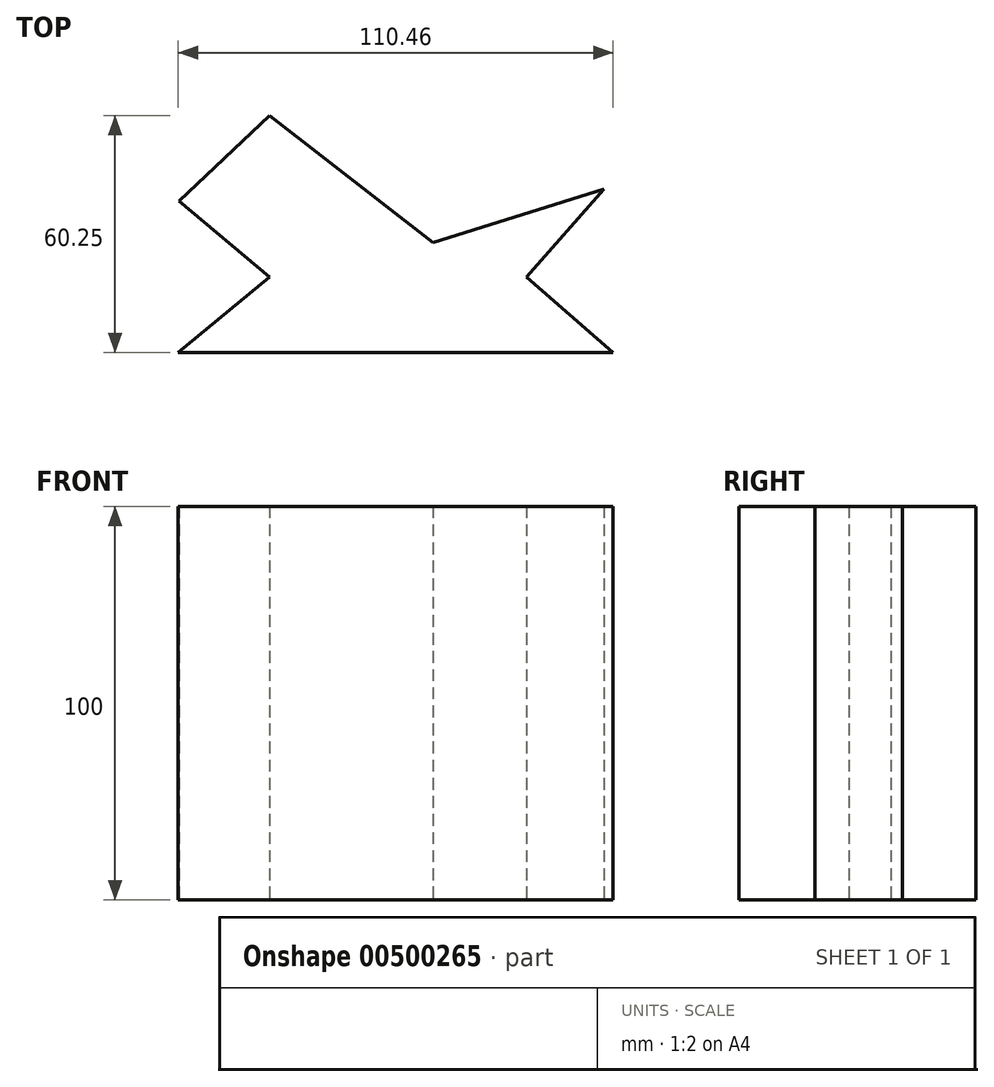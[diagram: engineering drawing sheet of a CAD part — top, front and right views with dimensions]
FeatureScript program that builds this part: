
annotation { "Feature Type Name" : "Feature", "Feature Type Description" : "" }
export const myFeature = defineFeature(function(context is Context, id is Id, definition is map)
    precondition{}
    {
        {
            var Q0;
            Q0=qCreatedBy(makeId("Top.planeOp"),FACE);
            var sketch = newSketch(context, id + "F0", { "sketchPlane" : qUnion([Q0])});
            skLineSegment(sketch, "E0", {"start": v(-41.49, 0) * mm, "end": v(-64.74, -19.3) * mm});
            skLineSegment(sketch, "E1", {"start": v(-41.49, 0) * mm, "end": v(-64.48, 19.3) * mm});
            skLineSegment(sketch, "E2", {"start": v(-64.74, -19.3) * mm, "end": v(45.72, -19.3) * mm});
            skLineSegment(sketch, "E3", {"start": v(45.72, -19.3) * mm, "end": v(23.78, 0) * mm});
            skLineSegment(sketch, "E4", {"start": v(23.78, 0) * mm, "end": v(43.4, 22.3) * mm});
            skLineSegment(sketch, "E5", {"start": v(43.4, 22.3) * mm, "end": v(0, 8.72) * mm});
            skLineSegment(sketch, "E6", {"start": v(0, 8.72) * mm, "end": v(-41.49, 40.96) * mm});
            skLineSegment(sketch, "E7", {"start": v(-41.49, 40.96) * mm, "end": v(-64.48, 19.3) * mm});
            skSolve(sketch);
        }
        {
            var Q0;
            Q0=makeQuery(id+"F0.imprint","IMPRINT",FACE,{"disambiguationData":[TD([[makeQuery(id+"F0.imprint","IMPRINT",EDGE,{"derivedFrom":sQuery(id+"F0.wireOp",EDGE,"E0")}),1.0]])]});
            extrude(context, id + "F1", {"entities" : qUnion([Q0]), "depth" : 100 * mm});
        }
    });
